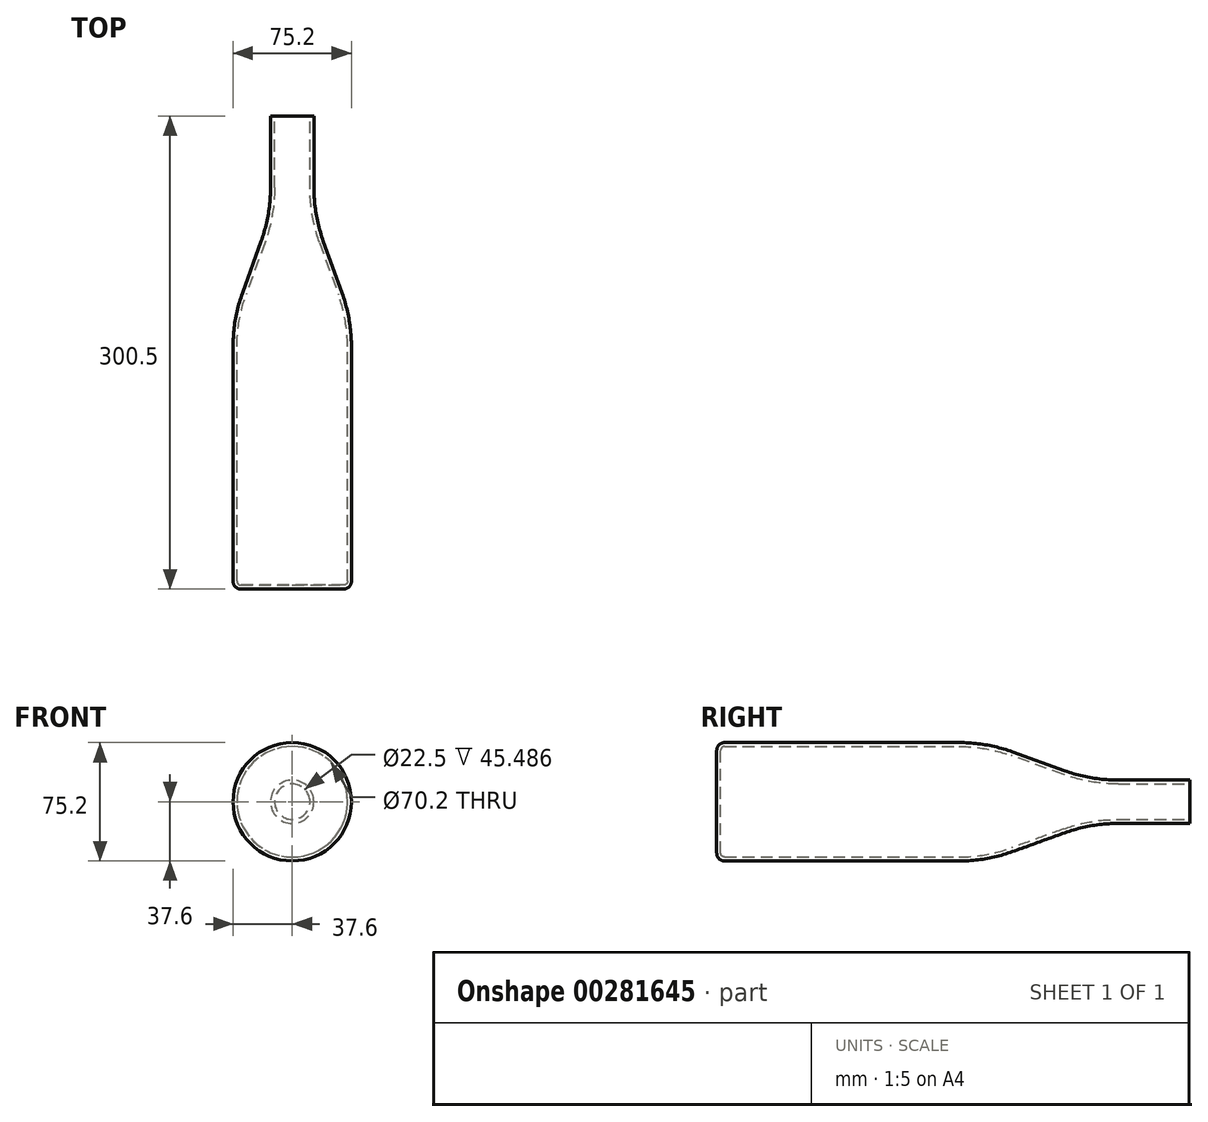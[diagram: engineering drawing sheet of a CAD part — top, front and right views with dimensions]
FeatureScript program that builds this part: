
annotation { "Feature Type Name" : "Feature", "Feature Type Description" : "" }
export const myFeature = defineFeature(function(context is Context, id is Id, definition is map)
    precondition{}
    {
        {
            var Q0;
            Q0=qCreatedBy(makeId("Top.planeOp"),FACE);
            var sketch = newSketch(context, id + "F0", { "sketchPlane" : qUnion([Q0])});
            skLineSegment(sketch, "E0", {"start": v(0, 0) * mm, "end": v(-13.75, 0) * mm});
            skLineSegment(sketch, "E1", {"start": v(-13.75, 0) * mm, "end": v(-13.75, -63) * mm});
            skLineSegment(sketch, "E2", {"start": v(-13.75, -63) * mm, "end": v(-37.6, -129) * mm});
            skLineSegment(sketch, "E3", {"start": v(-37.6, -129) * mm, "end": v(-37.6, -300.5) * mm});
            skLineSegment(sketch, "E4", {"start": v(-37.6, -300.5) * mm, "end": v(0, -300.5) * mm});
            skLineSegment(sketch, "E5", {"start": v(0, 0) * mm, "end": v(0, -300.5) * mm});
            skSolve(sketch);
        }
        {
            var Q0;
            Q0 = qSketchRegion(id + "F0", true);
            var Q1;
            Q1=sQuery(id+"F0.wireOp",EDGE,"E5");
            revolve(context, id + "F1", {"entities" : qUnion([Q0]), "axis" : qUnion([Q1]), "revolveType" : RevolveType.FULL});
        }
        {
            var Q0;
            Q0=makeQuery(id+"F1.opRevolve","SWEPT_EDGE",EDGE,{"disambiguationData":[OSD([sQuery(id+"F0.wireOp",EDGE,"E1"),sQuery(id+"F0.wireOp",EDGE,"E2")])]});
            var Q1;
            Q1=makeQuery(id+"F1.opRevolve","SWEPT_EDGE",EDGE,{"disambiguationData":[OSD([sQuery(id+"F0.wireOp",EDGE,"E2"),sQuery(id+"F0.wireOp",EDGE,"E3")])]});
            fillet(context, id + "F2", {"entities" : qUnion([Q0, Q1]), "radius" : 100 * mm, "tangentPropagation" : true});
        }
        {
            var Q0;
            Q0=makeQuery(id+"F1.opRevolve","SWEPT_EDGE",EDGE,{"disambiguationData":[OSD([sQuery(id+"F0.wireOp",EDGE,"E3"),sQuery(id+"F0.wireOp",EDGE,"E4")])]});
            fillet(context, id + "F3", {"entities" : qUnion([Q0]), "radius" : 5 * mm, "tangentPropagation" : true});
        }
        {
            var Q0;
            Q0=makeQuery(id+"F1.opRevolve","SWEPT_FACE",FACE,{"disambiguationData":[OSD([sQuery(id+"F0.wireOp",EDGE,"E0")])]});
            shell(context, id + "F4", {"entities" : qUnion([Q0]), "thickness" : 2.5 * mm});
        }
    });
